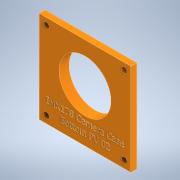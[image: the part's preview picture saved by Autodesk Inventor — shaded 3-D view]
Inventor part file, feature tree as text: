
AUTODESK INVENTOR PART (.ipt)
format: ipt  version: 2022.1 (Build 261234000, 234)  size: 828,416 bytes
history: native  units: mm
features: sketch x6, extrude x3, hole x2, emboss x1
ambient origin geometry x8: Origin, YZ Plane, XZ Plane, XY Plane, X Axis, Y Axis, Z Axis, Center Point
bodies: Body1 (feature_tree)
feature tree (12):
  extrude  "Extrusion11"  Depth=46.0mm
  extrude  "Extrusion13"  Depth=3.0mm
  hole  "HoleForScrews"  [1 undecoded]
  hole  "Hole2"  [1 undecoded]
  emboss  "Emboss3"
  extrude  "Extrusion14"  Depth=39.0mm
  sketch  "Sketch11"  dims[d63=46.0mm d64=46.0mm]
  sketch  "Sketch13"  dims[d65=3.0mm d66=0.0mm d73=26.0mm]
  sketch  "Sketch14"  dims[d74=26.0mm d75=41.0mm]
  sketch  "Sketch15"  dims[d76=41.0mm d77=2.0mm]
  sketch  "Sketch16"  dims[d78=0.0mm d79=39.0mm]
  sketch  "Sketch17"  dims[d80=39.0mm d81=3.0mm d82=4.369mm d83=4.369mm d84=2.0mm d85=14.3117mm d86=8.0mm d87=20.594885mm d88=3.0mm d89=26.0mm d90=6.0mm d91=4.0mm d92=2.0mm d93=90.0deg d94=8.0mm d95=20.594885mm d96=14.0mm d97=1.0mm d98=0.0mm d102=34.0mm d103=34.0mm d104=4.0mm d105=2.0mm d106=0.0mm]
note: 2 required parameter values undecoded (feature->parameter linkage not recoverable at this tier; creation-order binding heuristic only, values carry confidence <= 0.55)
